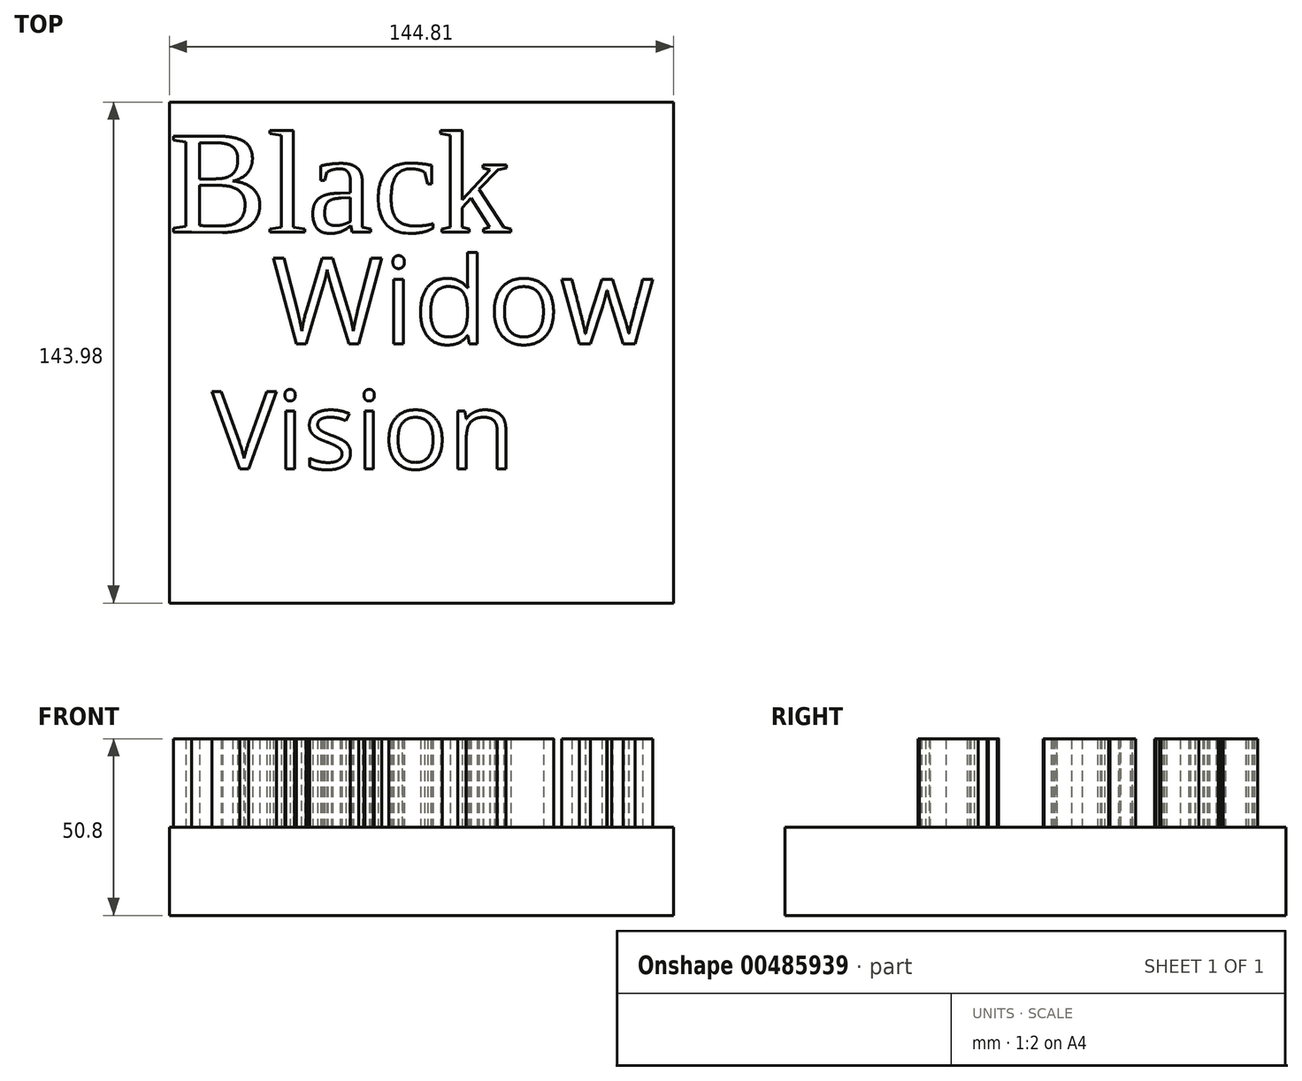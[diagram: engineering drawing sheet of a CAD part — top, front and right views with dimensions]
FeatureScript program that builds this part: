
annotation { "Feature Type Name" : "Feature", "Feature Type Description" : "" }
export const myFeature = defineFeature(function(context is Context, id is Id, definition is map)
    precondition{}
    {
        {
            var Q0;
            Q0=qCreatedBy(makeId("Top.planeOp"),FACE);
            var sketch = newSketch(context, id + "F0", { "sketchPlane" : qUnion([Q0])});
            skLineSegment(sketch, "E0.bottom", {"start": v(-71.37, 69.5) * mm, "end": v(73.44, 69.5) * mm});
            skLineSegment(sketch, "E0.top", {"start": v(-71.37, -74.48) * mm, "end": v(73.44, -74.48) * mm});
            skLineSegment(sketch, "E0.left", {"start": v(-71.37, 69.5) * mm, "end": v(-71.37, -74.48) * mm});
            skLineSegment(sketch, "E0.right", {"start": v(73.44, 69.5) * mm, "end": v(73.44, -74.48) * mm});
            skSolve(sketch);
        }
        {
            var Q0;
            Q0 = qSketchRegion(id + "F0", true);
            extrude(context, id + "F1", {"entities" : qUnion([Q0]), "depth" : 25.4 * mm});
        }
        {
            var Q0;
            Q0=makeQuery(id+"F1.opExtrude","CAP_FACE",FACE,{"disambiguationData":[OSD([sQuery(id+"F0.wireOp",EDGE,"E0.bottom"),sQuery(id+"F0.wireOp",EDGE,"E0.top"),sQuery(id+"F0.wireOp",EDGE,"E0.left"),sQuery(id+"F0.wireOp",EDGE,"E0.right")])],"isStart":false});
            var sketch = newSketch(context, id + "F2", { "sketchPlane" : qUnion([Q0])});
            skText(sketch, "E1", { "text": "Black", "fontName": "Tinos-Regular.ttf"});
            skText(sketch, "E2", { "text": "Widow", "fontName": "OpenSans-Regular.ttf"});
            skText(sketch, "E3", { "text": "Vision", "fontName": "OpenSans-Regular.ttf"});
            const initialGuessF2  = {"E1": [-0.07137, 0.03216, 1, 0, 0.03029], "E2": [-0.0419, 0, 1, 0, 0.0249], "E3": [-0.05913, -0.0359, 1, 0, 0.0224]};
            skSetInitialGuess(sketch, initialGuessF2);
            skSolve(sketch);
        }
        {
            var Q0;
            Q0=makeQuery(id+"F2.imprint","IMPRINT",FACE,{"disambiguationData":[TD([[makeQuery(id+"F2.imprint","IMPRINT",EDGE,{"derivedFrom":sQuery(id+"F2.wireOp",EDGE,"E1.sketch_text.stroke-0")}),-1.0]])]});
            var Q1;
            Q1=makeQuery(id+"F2.imprint","IMPRINT",FACE,{"disambiguationData":[TD([[makeQuery(id+"F2.imprint","IMPRINT",EDGE,{"derivedFrom":sQuery(id+"F2.wireOp",EDGE,"E1.sketch_text.stroke-30")}),-1.0]])]});
            var Q2;
            Q2=makeQuery(id+"F2.imprint","IMPRINT",FACE,{"disambiguationData":[TD([[makeQuery(id+"F2.imprint","IMPRINT",EDGE,{"derivedFrom":sQuery(id+"F2.wireOp",EDGE,"E1.sketch_text.stroke-40")}),-1.0]])]});
            var Q3;
            Q3=makeQuery(id+"F2.imprint","IMPRINT",FACE,{"disambiguationData":[TD([[makeQuery(id+"F2.imprint","IMPRINT",EDGE,{"derivedFrom":sQuery(id+"F2.wireOp",EDGE,"E1.sketch_text.stroke-68")}),-1.0]])]});
            var Q4;
            Q4=makeQuery(id+"F2.imprint","IMPRINT",FACE,{"disambiguationData":[TD([[makeQuery(id+"F2.imprint","IMPRINT",EDGE,{"derivedFrom":sQuery(id+"F2.wireOp",EDGE,"E1.sketch_text.stroke-83")}),-1.0]])]});
            extrude(context, id + "F3", {"entities" : qUnion([Q0, Q1, Q2, Q3, Q4]), "operationType" : NewBodyOperationType.ADD, "depth" : 25.4 * mm});
        }
        {
            var Q0;
            Q0=makeQuery(id+"F2.imprint","IMPRINT",FACE,{"disambiguationData":[TD([[makeQuery(id+"F2.imprint","IMPRINT",EDGE,{"derivedFrom":sQuery(id+"F2.wireOp",EDGE,"E2.sketch_text.stroke-0")}),-1.0]])]});
            extrude(context, id + "F4", {"entities" : qUnion([Q0]), "operationType" : NewBodyOperationType.ADD, "depth" : 25.4 * mm});
        }
        {
            var Q0;
            Q0=makeQuery(id+"F2.imprint","IMPRINT",FACE,{"disambiguationData":[TD([[makeQuery(id+"F2.imprint","IMPRINT",EDGE,{"derivedFrom":sQuery(id+"F2.wireOp",EDGE,"E2.sketch_text.stroke-24")}),-1.0]])]});
            var Q1;
            Q1=makeQuery(id+"F2.imprint","IMPRINT",FACE,{"disambiguationData":[TD([[makeQuery(id+"F2.imprint","IMPRINT",EDGE,{"derivedFrom":sQuery(id+"F2.wireOp",EDGE,"E2.sketch_text.stroke-20")}),-1.0]])]});
            var Q2;
            Q2=makeQuery(id+"F2.imprint","IMPRINT",FACE,{"disambiguationData":[TD([[makeQuery(id+"F2.imprint","IMPRINT",EDGE,{"derivedFrom":sQuery(id+"F2.wireOp",EDGE,"E2.sketch_text.stroke-32")}),-1.0]])]});
            extrude(context, id + "F5", {"entities" : qUnion([Q0, Q1, Q2]), "operationType" : NewBodyOperationType.ADD, "depth" : 25.4 * mm});
        }
        {
            var Q0;
            Q0=makeQuery(id+"F2.imprint","IMPRINT",FACE,{"disambiguationData":[TD([[makeQuery(id+"F2.imprint","IMPRINT",EDGE,{"derivedFrom":sQuery(id+"F2.wireOp",EDGE,"E2.sketch_text.stroke-56")}),-1.0]])]});
            extrude(context, id + "F6", {"entities" : qUnion([Q0]), "operationType" : NewBodyOperationType.ADD, "depth" : 25.4 * mm});
        }
        {
            var Q0;
            Q0=makeQuery(id+"F2.imprint","IMPRINT",FACE,{"disambiguationData":[TD([[makeQuery(id+"F2.imprint","IMPRINT",EDGE,{"derivedFrom":sQuery(id+"F2.wireOp",EDGE,"E2.sketch_text.stroke-73")}),-1.0]])]});
            extrude(context, id + "F7", {"entities" : qUnion([Q0]), "operationType" : NewBodyOperationType.ADD, "depth" : 25.4 * mm});
        }
        {
            var Q0;
            Q0=makeQuery(id+"F2.imprint","IMPRINT",FACE,{"disambiguationData":[TD([[makeQuery(id+"F2.imprint","IMPRINT",EDGE,{"derivedFrom":sQuery(id+"F2.wireOp",EDGE,"E3.sketch_text.stroke-0")}),-1.0]])]});
            var Q1;
            Q1=makeQuery(id+"F2.imprint","IMPRINT",FACE,{"disambiguationData":[TD([[makeQuery(id+"F2.imprint","IMPRINT",EDGE,{"derivedFrom":sQuery(id+"F2.wireOp",EDGE,"E3.sketch_text.stroke-9")}),-1.0]])]});
            var Q2;
            Q2=makeQuery(id+"F2.imprint","IMPRINT",FACE,{"disambiguationData":[TD([[makeQuery(id+"F2.imprint","IMPRINT",EDGE,{"derivedFrom":sQuery(id+"F2.wireOp",EDGE,"E3.sketch_text.stroke-13")}),-1.0]])]});
            var Q3;
            Q3=makeQuery(id+"F2.imprint","IMPRINT",FACE,{"disambiguationData":[TD([[makeQuery(id+"F2.imprint","IMPRINT",EDGE,{"derivedFrom":sQuery(id+"F2.wireOp",EDGE,"E3.sketch_text.stroke-21")}),-1.0]])]});
            var Q4;
            Q4=makeQuery(id+"F2.imprint","IMPRINT",FACE,{"disambiguationData":[TD([[makeQuery(id+"F2.imprint","IMPRINT",EDGE,{"derivedFrom":sQuery(id+"F2.wireOp",EDGE,"E3.sketch_text.stroke-50")}),-1.0]])]});
            var Q5;
            Q5=makeQuery(id+"F2.imprint","IMPRINT",FACE,{"disambiguationData":[TD([[makeQuery(id+"F2.imprint","IMPRINT",EDGE,{"derivedFrom":sQuery(id+"F2.wireOp",EDGE,"E3.sketch_text.stroke-46")}),-1.0]])]});
            var Q6;
            Q6=makeQuery(id+"F2.imprint","IMPRINT",FACE,{"disambiguationData":[TD([[makeQuery(id+"F2.imprint","IMPRINT",EDGE,{"derivedFrom":sQuery(id+"F2.wireOp",EDGE,"E3.sketch_text.stroke-58")}),-1.0]])]});
            extrude(context, id + "F8", {"entities" : qUnion([Q0, Q1, Q2, Q3, Q4, Q5, Q6]), "operationType" : NewBodyOperationType.ADD, "depth" : 25.4 * mm});
        }
        {
            var Q0;
            Q0=makeQuery(id+"F2.imprint","IMPRINT",FACE,{"disambiguationData":[TD([[makeQuery(id+"F2.imprint","IMPRINT",EDGE,{"derivedFrom":sQuery(id+"F2.wireOp",EDGE,"E3.sketch_text.stroke-75")}),-1.0]])]});
            extrude(context, id + "F9", {"entities" : qUnion([Q0]), "operationType" : NewBodyOperationType.ADD, "depth" : 25.4 * mm});
        }
    });
